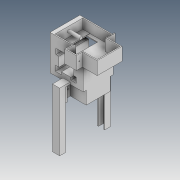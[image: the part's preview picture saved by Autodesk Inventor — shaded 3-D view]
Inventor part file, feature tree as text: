
AUTODESK INVENTOR PART (.ipt)
format: ipt  version: 2021 (Build 250183000, 183)  size: 735,744 bytes
history: native  units: in
note: dims shown in document units (in); Inventor stores cm internally (conversion verified against a paired STEP export)
features: sketch x39, extrude x38, fillet x2, other x1
ambient origin geometry x8: Origin, YZ Plane, XZ Plane, XY Plane, X Axis, Y Axis, Z Axis, Center Point
bodies: Body1 (feature_tree)
feature tree (80):
  other  "Sólido1"
  extrude  "Extrusão1"  Depth=0.1969in
  extrude  "Extrusão2"  Depth=0.3937in
  extrude  "Extrusão3"  Depth=0.0984in
  extrude  "Extrusão4"  Depth=0.1969in
  extrude  "Extrusão5"  Depth=0.3937in
  extrude  "Extrusão6"  Depth=0.0079in
  extrude  "Extrusão7"  Depth=0.0079in
  extrude  "Extrusão10"  Depth=0.0079in
  extrude  "Extrusão11"  Depth=0.0079in
  extrude  "Extrusão12"  Depth=0.0079in
  extrude  "Extrusão13"  Depth=0.0079in
  extrude  "Extrusão25"  Depth=0.0079in
  extrude  "Extrusão26"  Depth=0.0079in
  extrude  "Extrusão27"  Depth=0.1575in
  extrude  "Extrusão28"  Depth=0.0079in
  extrude  "Extrusão29"  Depth=0.0394in
  extrude  "Extrusão30"  Depth=0.0787in
  extrude  "Extrusão31"  Depth=1.1811in TaperAngle=0.0deg
  extrude  "Extrusão32"  Depth=0.3543in
  extrude  "Extrusão34"  Depth=0.1181in
  extrude  "Extrusão35"  Depth=0.1969in TaperAngle=0.0deg
  extrude  "Extrusão36"  Depth=0.0591in
  extrude  "Extrusão37"  Depth=0.2559in
  extrude  "Extrusão38"  Depth=0.0315in TaperAngle=0.0deg
  extrude  "Extrusão39"  Depth=0.0394in
  extrude  "Extrusão41"  Depth=0.0394in
  extrude  "Extrusão43"  Depth=0.0394in
  extrude  "Extrusão44"  Depth=0.0394in
  extrude  "Extrusão46"  Depth=0.0394in TaperAngle=0.0deg
  extrude  "Extrusão47"  Depth=0.1378in
  fillet  "Arredondamento5"  Radius=0.6496in
  fillet  "Arredondamento6"  Radius=0.6496in
  extrude  "Extrusão48"  Depth=0.6693in
  extrude  "Extrusão49"  Depth=0.4724in TaperAngle=0.0deg
  extrude  "Extrusão50"  Depth=0.0394in
  extrude  "Extrusão51"  Depth=0.1969in TaperAngle=0.0deg
  extrude  "Extrusão52"  Depth=0.0394in
  extrude  "Extrusão53"  Depth=0.0394in
  extrude  "Extrusão54"  Depth=0.0787in
  extrude  "Extrusão55"  Depth=0.0787in
  sketch  "Esboço84"  dims[d156=0.0197in d157=0.0197in d158=0.0787in d159=0.1181in d160=0.0in d161=0.0394in d162=0.1181in d163=0.0394in d164=0.0in d165=0.0in d169=0.0787in d170=0.0315in d171=0.0in d172=0.3937in d173=0.0in d175=0.1181in d176=0.4803in d177=0.0in d178=0.4803in d179=0.0in d180=0.1181in d181=0.1181in d182=0.0394in d183=0.0in d184=0.3724in d185=0.4528in d186=0.8661in d187=0.4528in d188=0.0394in d189=0.0in d199=0.3937in d200=0.0in d206=0.4724in d207=0.0in d208=0.0394in d209=0.0in d210=0.0197in d218=0.0787in d219=0.0787in d220=0.0787in d221=0.0787in d222=0.0787in d223=0.0394in d224=0.0in d225=0.0394in d226=0.0394in d227=0.0394in d228=0.0394in d229=0.0394in d230=0.0394in d231=0.0394in d232=0.4724in d233=0.0in d234=0.0787in d235=0.0787in d236=0.0394in d237=0.0394in d238=0.4724in d239=0.0in d240=0.0394in d241=0.0in d242=0.0394in d243=0.2362in d244=0.0394in d245=0.0394in d246=0.0in d247=0.5512in d248=0.374in d249=0.2047in d250=0.374in d251=0.0787in d252=0.0in d253=0.0394in d254=0.0394in d255=0.0394in d256=0.0394in d257=0.0394in d258=0.0394in d259=0.0394in d260=0.0in d261=2.2441in d262=0.0in d263=0.0394in d264=0.0in d265=0.5906in d266=0.0in d94=0.0197in d95=0.0344in d96=0.0197in d97=0.0344in d123=0.0197in d124=0.0344in d125=0.0197in d126=0.0344in d167=0.0197in d168=0.0344in]
  sketch  "Esboço2"  dims[d0=0.1969in d1=0.1969in]
  sketch  "Esboço4"  dims[d2=0.1181in d3=0.3937in]
  sketch  "Esboço5"  dims[d4=0.1969in d5=0.0984in]
  sketch  "Esboço6"  dims[d6=0.3937in d7=0.1969in]
  sketch  "Esboço7"  dims[d8=0.1969in d9=0.3937in]
  sketch  "Esboço8"  dims[d11=0.1969in d12=0.0079in]
  sketch  "Esboço10"  dims[d13=0.0079in d14=0.0079in]
  sketch  "Esboço15"  dims[d15=0.0079in d16=0.0079in]
  sketch  "Esboço16"  dims[d17=0.0079in d19=0.0079in]
  sketch  "Esboço18"  dims[d20=0.0079in d21=0.0079in]
  sketch  "Esboço20"  dims[d22=0.0079in d23=0.0079in]
  sketch  "Esboço38"  dims[d24=0.0079in d25=0.0079in]
  sketch  "Esboço39"  dims[d26=0.0079in d27=0.0079in]
  sketch  "Esboço40"  dims[d28=0.2756in d29=0.1575in]
  sketch  "Esboço41"  dims[d30=0.2756in d31=0.0079in]
  sketch  "Esboço42"  dims[d32=0.0787in d33=0.0394in]
  sketch  "Esboço46"  dims[d34=0.0079in d35=0.0787in]
  sketch  "Esboço47"  dims[d36=0.0394in d37=1.1811in d38=0.0in]
  sketch  "Esboço48"  dims[d39=0.4724in d40=0.3543in]
  sketch  "Esboço53"  dims[d46=0.1969in d47=0.0in d48=0.1181in]
  sketch  "Esboço54"  dims[d49=0.4803in d50=0.0in d51=0.1969in d52=0.0in]
  sketch  "Esboço57"  dims[d53=0.1969in d54=0.0in d55=0.0591in]
  sketch  "Esboço58"  dims[d56=0.1969in d57=0.0in d58=0.2559in]
  sketch  "Esboço59"  dims[d59=0.2559in d60=0.0315in d61=0.0in]
  sketch  "Esboço60"  dims[d68=0.1181in d69=0.0in d70=0.0394in]
  sketch  "Esboço62"  dims[d71=0.0394in d73=0.0394in]
  sketch  "Esboço64"  dims[d74=0.3937in d75=0.0in d76=0.0394in]
  sketch  "Esboço65"  dims[d77=0.0in d78=0.0in d79=0.0394in]
  sketch  "Esboço67"  dims[d80=0.0394in d81=0.0394in d82=0.0in]
  sketch  "Esboço68"  dims[d128=0.1378in d129=0.1378in d131=0.6496in d132=0.6496in]
  sketch  "Esboço69"  dims[d133=0.0197in d134=0.6693in]
  sketch  "Esboço71"  dims[d135=0.0197in d136=0.4724in d137=0.0in]
  sketch  "Esboço72"  dims[d138=0.0394in d139=0.0in d140=0.0394in]
  sketch  "Esboço78"  dims[d141=0.1969in d142=0.0in d143=0.1969in d144=0.0in]
  sketch  "Esboço79"  dims[d145=0.2323in d146=0.0394in]
  sketch  "Esboço80"  dims[d147=0.1083in d148=0.0394in]
  sketch  "Esboço81"  dims[d149=0.1969in d150=0.0in d152=0.0787in]
  sketch  "Esboço82"  dims[d153=0.0394in d154=0.0in d155=0.0787in]
